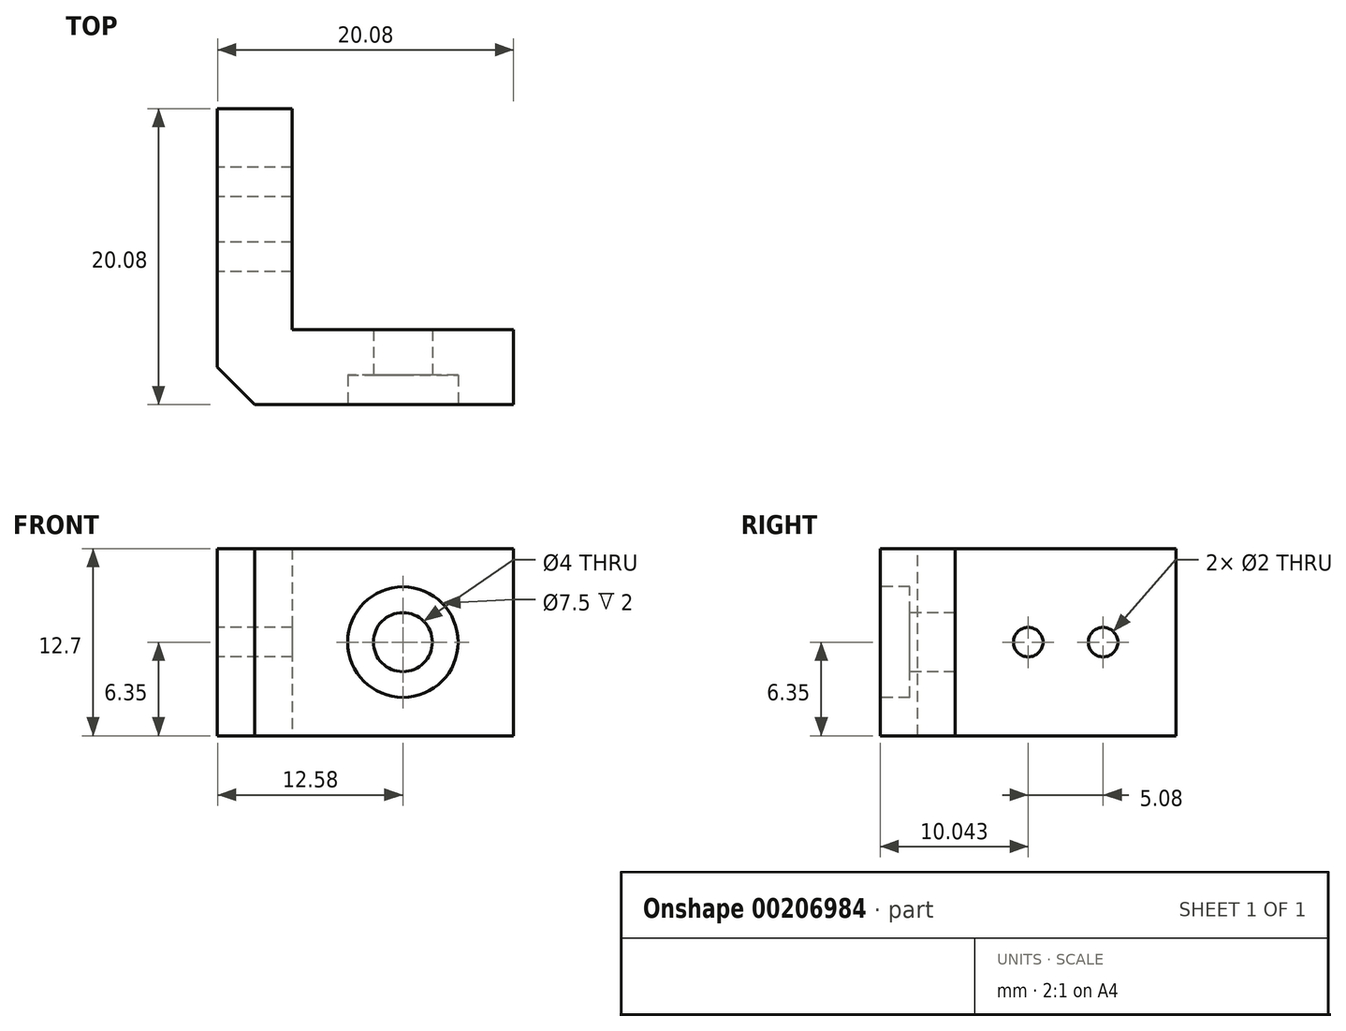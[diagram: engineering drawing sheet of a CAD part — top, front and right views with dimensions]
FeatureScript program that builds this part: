
annotation { "Feature Type Name" : "Feature", "Feature Type Description" : "" }
export const myFeature = defineFeature(function(context is Context, id is Id, definition is map)
    precondition{}
    {
        {
            var Q0;
            Q0=qCreatedBy(makeId("Top.planeOp"),FACE);
            var sketch = newSketch(context, id + "F0", { "sketchPlane" : qUnion([Q0])});
            skLineSegment(sketch, "E0", {"start": v(5.87, 17.41) * mm, "end": v(5.87, -2.67) * mm});
            skLineSegment(sketch, "E1", {"start": v(5.87, -2.67) * mm, "end": v(25.95, -2.67) * mm});
            skLineSegment(sketch, "E2", {"start": v(25.95, -2.67) * mm, "end": v(25.95, 2.41) * mm});
            skLineSegment(sketch, "E3", {"start": v(25.95, 2.41) * mm, "end": v(10.95, 2.41) * mm});
            skLineSegment(sketch, "E4", {"start": v(10.95, 2.41) * mm, "end": v(10.95, 17.41) * mm});
            skLineSegment(sketch, "E5", {"start": v(10.95, 17.41) * mm, "end": v(5.87, 17.41) * mm});
            skSolve(sketch);
        }
        {
            var Q0;
            Q0=makeQuery(id+"F0.imprint","IMPRINT",FACE,{"disambiguationData":[TD([[makeQuery(id+"F0.imprint","IMPRINT",EDGE,{"derivedFrom":sQuery(id+"F0.wireOp",EDGE,"E0")}),1.0]])]});
            extrude(context, id + "F1", {"entities" : qUnion([Q0]), "depth" : 12.7 * mm});
        }
        {
            var Q0;
            Q0=makeQuery(id+"F1.opExtrude","SWEPT_FACE",FACE,{"disambiguationData":[OSD([sQuery(id+"F0.wireOp",EDGE,"E1")])]});
            var sketch = newSketch(context, id + "F2", { "sketchPlane" : qUnion([Q0])});
            skPoint(sketch, "E6.0", {"position": v(18.45, 12.7) * mm});
            skPoint(sketch, "E7", {"position": v(18.45, 6.35) * mm});
            skPoint(sketch, "E7.positionSnap0", {"position": v(25.95, 6.35) * mm});
            skSolve(sketch);
        }
        {
            var Q0;
            Q0=sQuery(id+"F2.wireOp",VERTEX,"E7");
            var Q1;
            Q1=makeQuery(id+"F1.opExtrude","SWEPT_BODY",BODY,{"disambiguationData":[OSD([sQuery(id+"F0.wireOp",EDGE,"E0"),sQuery(id+"F0.wireOp",EDGE,"E1"),sQuery(id+"F0.wireOp",EDGE,"E2"),sQuery(id+"F0.wireOp",EDGE,"E3"),sQuery(id+"F0.wireOp",EDGE,"E4"),sQuery(id+"F0.wireOp",EDGE,"E5")])]});
            hole(context, id + "F3", {"style" : HoleStyle.C_BORE, "endStyle" : HoleEndStyle.BLIND, "holeDiameter" : 4 * mm, "cBoreDiameter" : 7.5 * mm, "cBoreDepth" : 2 * mm, "holeDepth" : 12.7 * mm, "locations" : qUnion([Q0]), "scope" : qUnion([Q1])});
        }
        {
            var Q0;
            Q0=makeQuery(id+"F1.opExtrude","SWEPT_EDGE",EDGE,{"disambiguationData":[OSD([sQuery(id+"F0.wireOp",EDGE,"E0"),sQuery(id+"F0.wireOp",EDGE,"E1")])]});
            chamfer(context, id + "F4", {"entities" : qUnion([Q0]), "width" : 2.54 * mm, "tangentPropagation" : true});
        }
        {
            var Q0;
            Q0=makeQuery(id+"F1.opExtrude","SWEPT_FACE",FACE,{"disambiguationData":[OSD([sQuery(id+"F0.wireOp",EDGE,"E0")])]});
            var sketch = newSketch(context, id + "F5", { "sketchPlane" : qUnion([Q0])});
            skLineSegment(sketch, "E8.0", {"start": v(-2.41, 12.7) * mm, "end": v(-17.41, 12.7) * mm});
            skLineSegment(sketch, "E9", {"start": v(-2.41, 12.7) * mm, "end": v(-2.41, 0) * mm, "construction": true});
            skPoint(sketch, "E10", {"position": v(-12.45, 6.35) * mm});
            skPoint(sketch, "E10.positionSnap0", {"position": v(-17.41, 6.35) * mm});
            skPoint(sketch, "E11", {"position": v(-7.37, 6.35) * mm});
            skLineSegment(sketch, "E12", {"start": v(-12.45, 6.35) * mm, "end": v(-17.41, 6.35) * mm, "construction": true});
            skLineSegment(sketch, "E13", {"start": v(-7.37, 6.35) * mm, "end": v(-2.41, 6.35) * mm, "construction": true});
            skSolve(sketch);
        }
        {
            var Q0;
            Q0=sQuery(id+"F5.wireOp",VERTEX,"E11");
            var Q1;
            Q1=sQuery(id+"F5.wireOp",VERTEX,"E10");
            var Q2;
            Q2=makeQuery(id+"F1.opExtrude","SWEPT_BODY",BODY,{"disambiguationData":[OSD([sQuery(id+"F0.wireOp",EDGE,"E0"),sQuery(id+"F0.wireOp",EDGE,"E1"),sQuery(id+"F0.wireOp",EDGE,"E2"),sQuery(id+"F0.wireOp",EDGE,"E3"),sQuery(id+"F0.wireOp",EDGE,"E4"),sQuery(id+"F0.wireOp",EDGE,"E5")])]});
            hole(context, id + "F6", {"style" : HoleStyle.SIMPLE, "endStyle" : HoleEndStyle.THROUGH, "holeDiameter" : 2 * mm, "locations" : qUnion([Q0, Q1]), "scope" : qUnion([Q2]), "isTappedThrough" : true});
        }
    });
